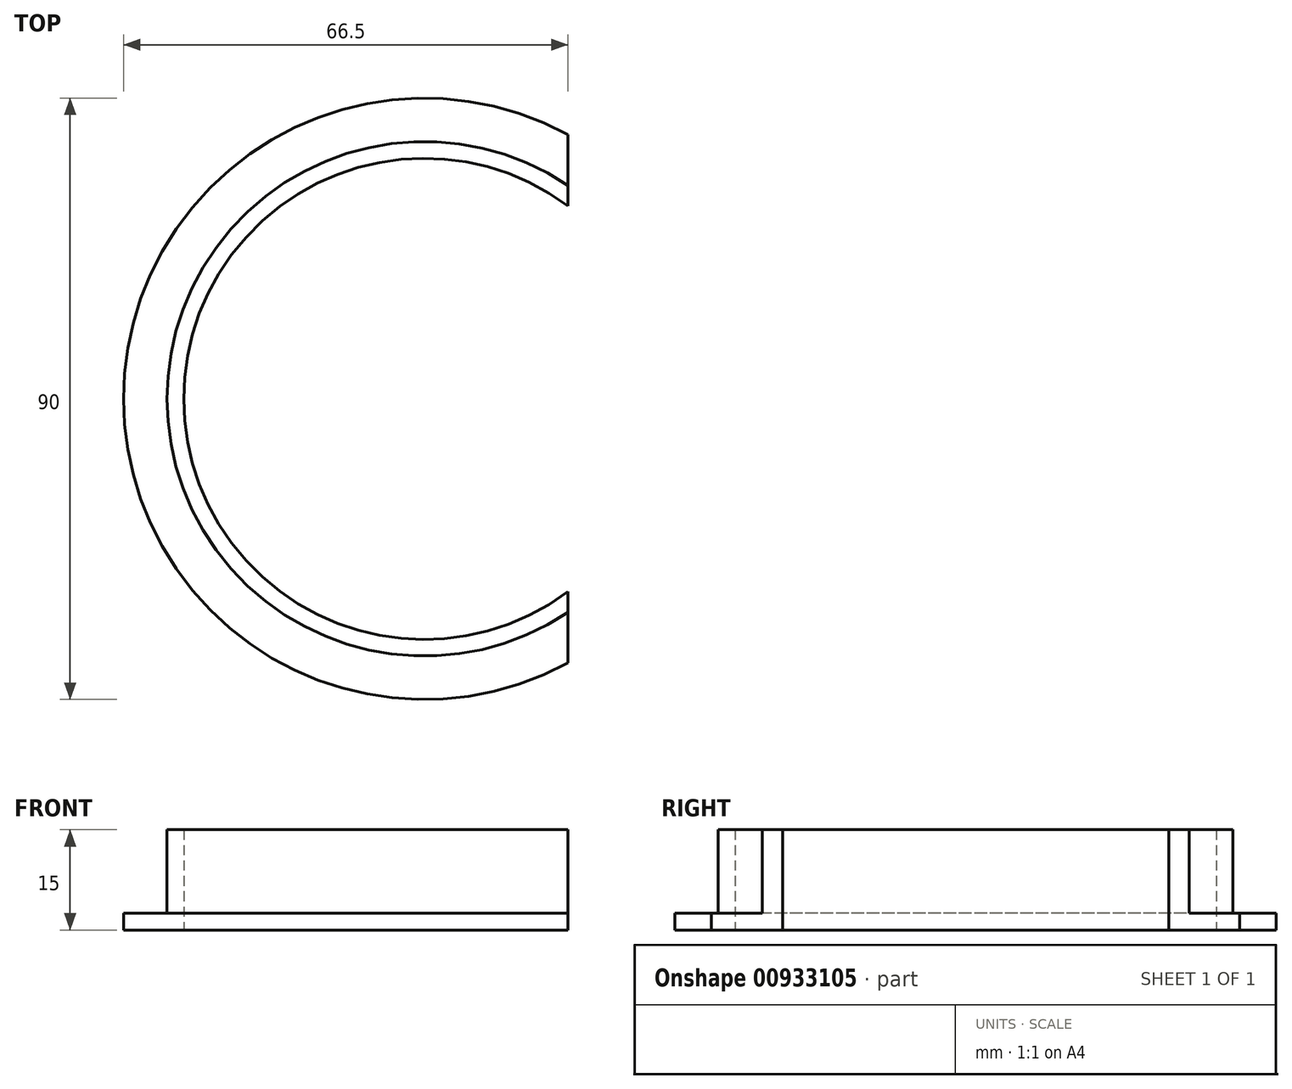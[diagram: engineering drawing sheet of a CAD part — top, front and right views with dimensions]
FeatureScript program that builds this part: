
annotation { "Feature Type Name" : "Feature", "Feature Type Description" : "" }
export const myFeature = defineFeature(function(context is Context, id is Id, definition is map)
    precondition{}
    {
        {
            var Q0;
            Q0=qCreatedBy(makeId("Top.planeOp"),FACE);
            var sketch = newSketch(context, id + "F0", { "sketchPlane" : qUnion([Q0])});
            skCircle(sketch, "E0", {"center": v(0, 0) * mm, "radius": 38.5 * mm});
            skLineSegment(sketch, "E1", {"start": v(-60.76, 0) * mm, "end": v(66.74, 0) * mm, "construction": true});
            skLineSegment(sketch, "E2", {"start": v(21.5, 52.57) * mm, "end": v(21.5, -65.16) * mm});
            skLineSegment(sketch, "E3", {"start": v(21.5, 31.94) * mm, "end": v(21.5, -31.94) * mm});
            skCircle(sketch, "E4", {"center": v(0, 0) * mm, "radius": 45 * mm});
            skCircle(sketch, "E5", {"center": v(0, 0) * mm, "radius": 36 * mm});
            skSolve(sketch);
        }
        {
            var Q0;
            {var subQ0=sQuery(id+"F0.wireOp",EDGE,"E3");var subQ5=sQuery(id+"F0.wireOp",EDGE,"E5");var subQ6=makeQuery(id+"F0.imprint","INTERSECT",VERTEX,{"disambiguationData":[OD(0.0)],"derivedFrom":[subQ0,subQ5]});Q0=makeQuery(id+"F0.imprint","IMPRINT",FACE,{"disambiguationData":[TD([[makeQuery(id+"F0.imprint","IMPRINT",EDGE,{"disambiguationData":[TD([[subQ6,-1.0]])],"derivedFrom":subQ5}),-1.0]])]});}
            var Q1;
            Q1=sQuery(id+"F0.wireOp",EDGE,"E0");
            extrude(context, id + "F1", {"entities" : qUnion([Q0]), "surfaceEntities" : qUnion([Q1]), "depth" : 15 * mm, "offsetDistance" : 25 * mm});
        }
        {
            var Q0;
            {var subQ1=sQuery(id+"F0.wireOp",EDGE,"E2");var subQ5=sQuery(id+"F0.wireOp",EDGE,"E4");var subQ6=makeQuery(id+"F0.imprint","INTERSECT",VERTEX,{"disambiguationData":[OD(0.0)],"derivedFrom":[subQ1,subQ5]});Q0=makeQuery(id+"F0.imprint","IMPRINT",FACE,{"disambiguationData":[TD([[makeQuery(id+"F0.imprint","IMPRINT",EDGE,{"disambiguationData":[TD([[subQ6,-1.0]])],"derivedFrom":subQ5}),1.0]])]});}
            var Q1;
            {var subQ0=sQuery(id+"F0.wireOp",EDGE,"E5");var subQ1=sQuery(id+"F0.wireOp",EDGE,"E3");var subQ2=makeQuery(id+"F0.imprint","INTERSECT",VERTEX,{"disambiguationData":[OD(0.0)],"derivedFrom":[subQ1,subQ0]});Q1=makeQuery(id+"F0.imprint","IMPRINT",FACE,{"disambiguationData":[TD([[makeQuery(id+"F0.imprint","IMPRINT",EDGE,{"disambiguationData":[TD([[subQ2,-1.0]])],"derivedFrom":subQ1}),-1.0]])]});}
            extrude(context, id + "F2", {"entities" : qUnion([Q0, Q1]), "operationType" : NewBodyOperationType.ADD, "depth" : 2.5 * mm, "offsetDistance" : 25 * mm});
        }
    });
